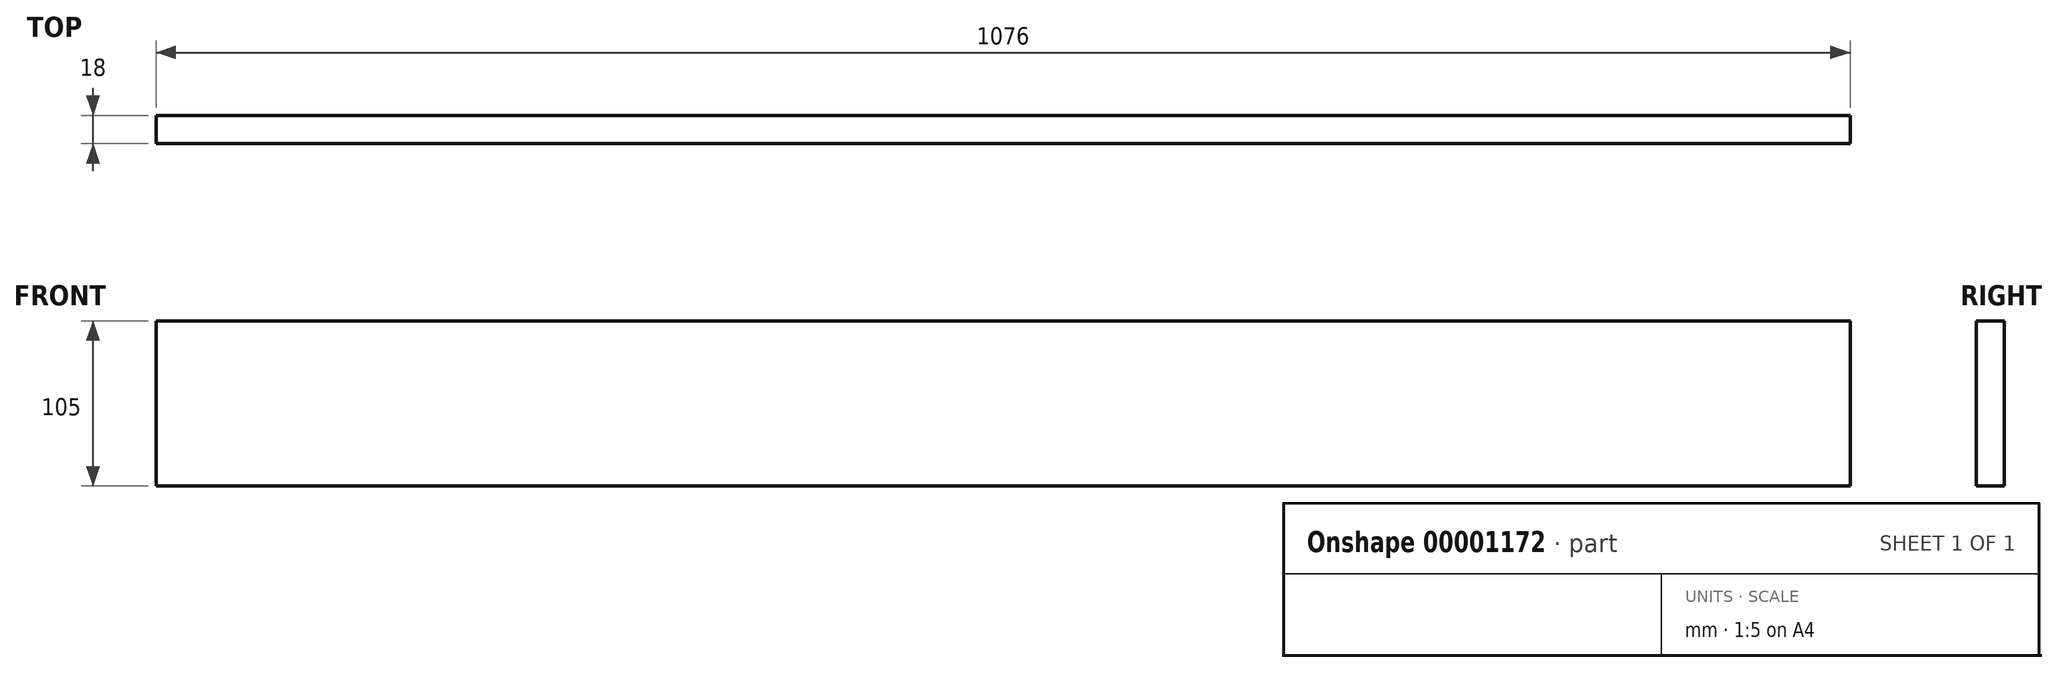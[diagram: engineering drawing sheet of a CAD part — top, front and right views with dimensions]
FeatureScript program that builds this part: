
annotation { "Feature Type Name" : "Feature", "Feature Type Description" : "" }
export const myFeature = defineFeature(function(context is Context, id is Id, definition is map)
    precondition{}
    {
        {
            var Q0;
            Q0=qCreatedBy(makeId("Front.planeOp"),FACE);
            var sketch = newSketch(context, id + "F0", { "sketchPlane" : qUnion([Q0])});
            skLineSegment(sketch, "E0", {"start": v(0, 0) * mm, "end": v(1076, 0) * mm});
            skLineSegment(sketch, "E1", {"start": v(1076, 0) * mm, "end": v(1076, 105) * mm});
            skLineSegment(sketch, "E2", {"start": v(1076, 105) * mm, "end": v(0, 105) * mm});
            skLineSegment(sketch, "E3", {"start": v(0, 105) * mm, "end": v(0, 0) * mm});
            skSolve(sketch);
        }
        {
            var Q0;
            Q0 = qSketchRegion(id + "F0", true);
            extrude(context, id + "F1", {"entities" : qUnion([Q0]), "depth" : 18 * mm});
        }
    });
